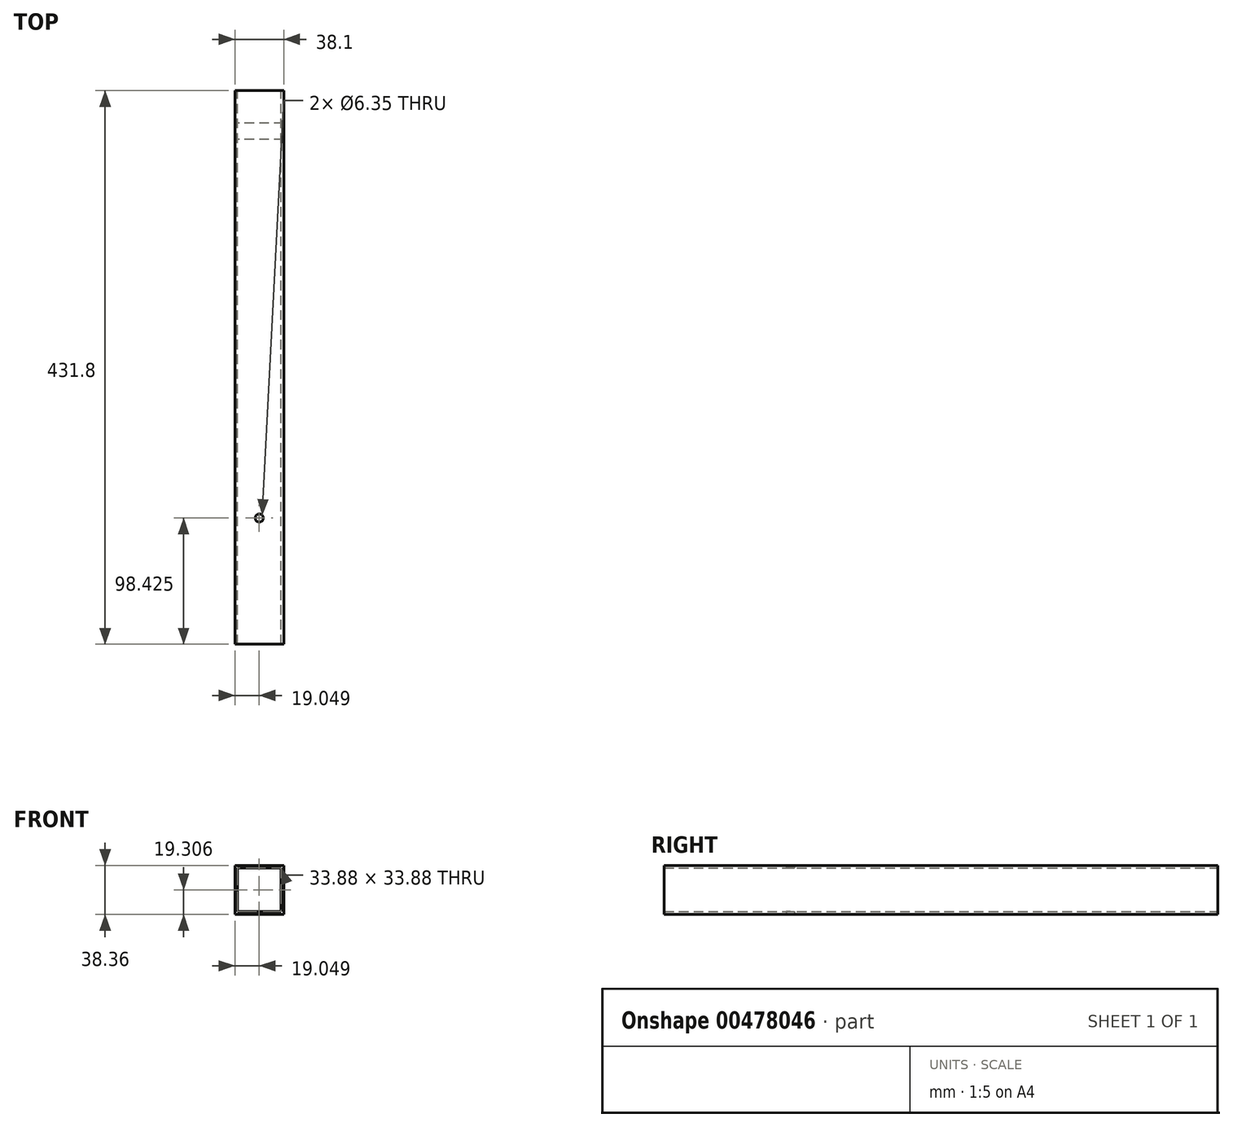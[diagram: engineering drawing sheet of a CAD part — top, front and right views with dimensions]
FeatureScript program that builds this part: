
annotation { "Feature Type Name" : "Feature", "Feature Type Description" : "" }
export const myFeature = defineFeature(function(context is Context, id is Id, definition is map)
    precondition{}
    {
        {
            var Q0;
            Q0=qCreatedBy(makeId("Front.planeOp"),FACE);
            var sketch = newSketch(context, id + "F0", { "sketchPlane" : qUnion([Q0])});
            skLineSegment(sketch, "E0.bottom", {"start": v(-64.17, 38.35) * mm, "end": v(-26.07, 38.35) * mm});
            skLineSegment(sketch, "E0.top", {"start": v(-64.17, 0.25) * mm, "end": v(-26.07, 0.25) * mm});
            skLineSegment(sketch, "E0.left", {"start": v(-64.17, 38.35) * mm, "end": v(-64.17, 0.25) * mm});
            skLineSegment(sketch, "E0.right", {"start": v(-26.07, 38.35) * mm, "end": v(-26.07, 0.25) * mm});
            skLineSegment(sketch, "E1.0", {"start": v(-28.18, 36.24) * mm, "end": v(-28.18, 2.35) * mm});
            skLineSegment(sketch, "E1.1", {"start": v(-62.06, 36.24) * mm, "end": v(-28.18, 36.24) * mm});
            skLineSegment(sketch, "E1.2", {"start": v(-62.06, 36.24) * mm, "end": v(-62.06, 2.35) * mm});
            skLineSegment(sketch, "E1.3", {"start": v(-62.06, 2.35) * mm, "end": v(-28.18, 2.35) * mm});
            skSolve(sketch);
        }
        {
            var Q0;
            Q0=makeQuery(id+"F0.imprint","IMPRINT",FACE,{"disambiguationData":[TD([[makeQuery(id+"F0.imprint","IMPRINT",EDGE,{"derivedFrom":sQuery(id+"F0.wireOp",EDGE,"E0.bottom")}),-1.0]])]});
            extrude(context, id + "F1", {"entities" : qUnion([Q0]), "depth" : 431.8 * mm});
        }
        {
            var Q0;
            Q0=makeQuery(id+"F1.opExtrude","SWEPT_FACE",FACE,{"disambiguationData":[OSD([sQuery(id+"F0.wireOp",EDGE,"E0.top")])]});
            var sketch = newSketch(context, id + "F2", { "sketchPlane" : qUnion([Q0])});
            skLineSegment(sketch, "E2", {"start": v(-26.07, 38.1) * mm, "end": v(-64.17, 38.1) * mm});
            skLineSegment(sketch, "E3", {"start": v(-26.07, 38.1) * mm, "end": v(-26.07, 25.4) * mm});
            skLineSegment(sketch, "E4", {"start": v(-26.07, 25.4) * mm, "end": v(-64.17, 25.4) * mm});
            skLineSegment(sketch, "E5", {"start": v(-64.17, 25.4) * mm, "end": v(-64.17, 38.1) * mm});
            skSolve(sketch);
        }
        {
            var Q0;
            Q0=qSketchRegion(id+"F2",true);
            extrude(context, id + "F3", {"entities" : qUnion([Q0]), "operationType" : NewBodyOperationType.ADD, "depth" : 0.25 * mm});
        }
        {
            var Q0;
            {var subQ2=sQuery(id+"F0.wireOp",EDGE,"E0.top");Q0=makeQuery(id+"F3.boolean.opBoolean","SPLIT",FACE,{"disambiguationData":[TD([makeQuery(id+"F3.opExtrude","SWEPT_FACE",FACE,{"disambiguationData":[OSD([sQuery(id+"F2.wireOp",EDGE,"E2")])]})])],"derivedFrom":makeQuery(id+"F1.opExtrude","SWEPT_FACE",FACE,{"disambiguationData":[OSD([subQ2])]})});}
            var sketch = newSketch(context, id + "F4", { "sketchPlane" : qUnion([Q0])});
            skCircle(sketch, "E6", {"center": v(-45.12, 333.38) * mm, "radius": 3.18 * mm});
            skPoint(sketch, "E6.centerSnap0", {"position": v(-45.12, 431.8) * mm});
            skSolve(sketch);
        }
        {
            var Q0;
            Q0=qSketchRegion(id+"F4",true);
            extrude(context, id + "F5", {"entities" : qUnion([Q0]), "operationType" : NewBodyOperationType.REMOVE, "oppositeDirection" : true, "depth" : 76.2 * mm});
        }
    });
